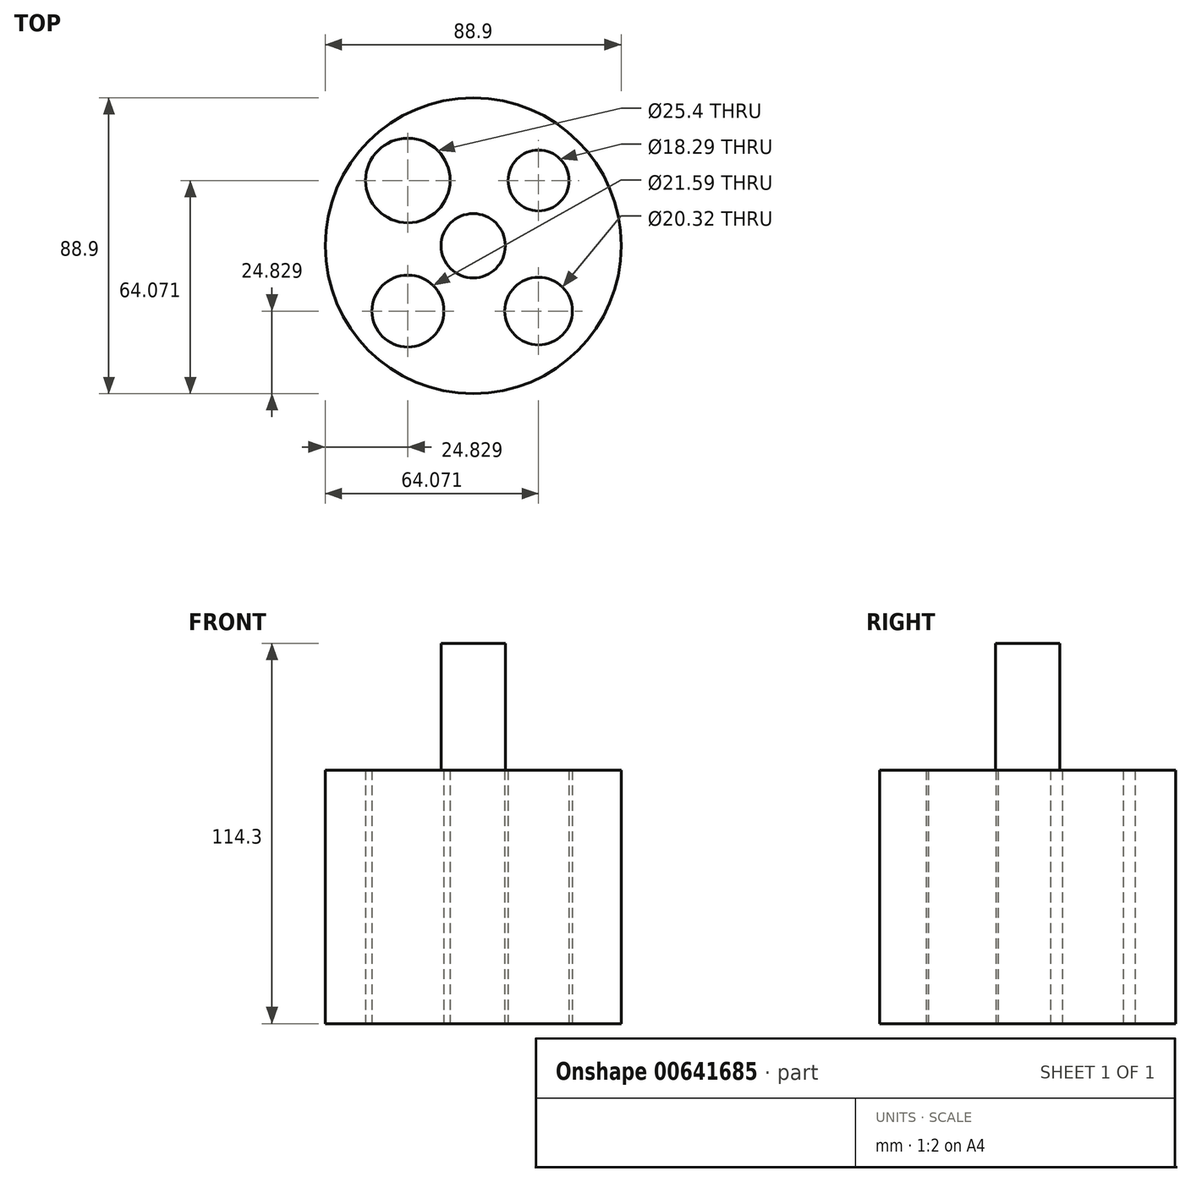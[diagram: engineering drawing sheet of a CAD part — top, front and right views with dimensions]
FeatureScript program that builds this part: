
annotation { "Feature Type Name" : "Feature", "Feature Type Description" : "" }
export const myFeature = defineFeature(function(context is Context, id is Id, definition is map)
    precondition{}
    {
        {
            var Q0;
            Q0=qCreatedBy(makeId("Top.planeOp"),FACE);
            var sketch = newSketch(context, id + "F0", { "sketchPlane" : qUnion([Q0])});
            skCircle(sketch, "E0", {"center": v(0, 0) * mm, "radius": 44.45 * mm});
            skCircle(sketch, "E1", {"center": v(-19.62, 19.62) * mm, "radius": 12.7 * mm});
            skCircle(sketch, "E2", {"center": v(19.62, 19.62) * mm, "radius": 9.14 * mm});
            skCircle(sketch, "E3", {"center": v(-19.62, -19.62) * mm, "radius": 10.8 * mm});
            skCircle(sketch, "E4", {"center": v(19.62, -19.62) * mm, "radius": 10.16 * mm});
            skSolve(sketch);
        }
        {
            var Q0;
            Q0=makeQuery(id+"F0.imprint","IMPRINT",FACE,{"disambiguationData":[TD([[makeQuery(id+"F0.imprint","IMPRINT",EDGE,{"derivedFrom":sQuery(id+"F0.wireOp",EDGE,"E0")}),1.0]])]});
            extrude(context, id + "F1", {"entities" : qUnion([Q0]), "depth" : 76.2 * mm, "offsetDistance" : 25.4 * mm});
        }
        {
            var Q0;
            Q0=makeQuery(id+"F1.opExtrude","CAP_FACE",FACE,{"disambiguationData":[OSD([sQuery(id+"F0.wireOp",EDGE,"E0"),sQuery(id+"F0.wireOp",EDGE,"E1"),sQuery(id+"F0.wireOp",EDGE,"E2"),sQuery(id+"F0.wireOp",EDGE,"E3"),sQuery(id+"F0.wireOp",EDGE,"E4")])],"isStart":false});
            var sketch = newSketch(context, id + "F2", { "sketchPlane" : qUnion([Q0])});
            skCircle(sketch, "E5", {"center": v(0, 0) * mm, "radius": 9.65 * mm});
            skSolve(sketch);
        }
        {
            var Q0;
            Q0=makeQuery(id+"F2.imprint","IMPRINT",FACE,{"disambiguationData":[TD([[makeQuery(id+"F2.imprint","IMPRINT",EDGE,{"derivedFrom":sQuery(id+"F2.wireOp",EDGE,"E5")}),1.0]])]});
            extrude(context, id + "F3", {"entities" : qUnion([Q0]), "operationType" : NewBodyOperationType.ADD, "depth" : 38.1 * mm, "offsetDistance" : 25.4 * mm});
        }
    });
